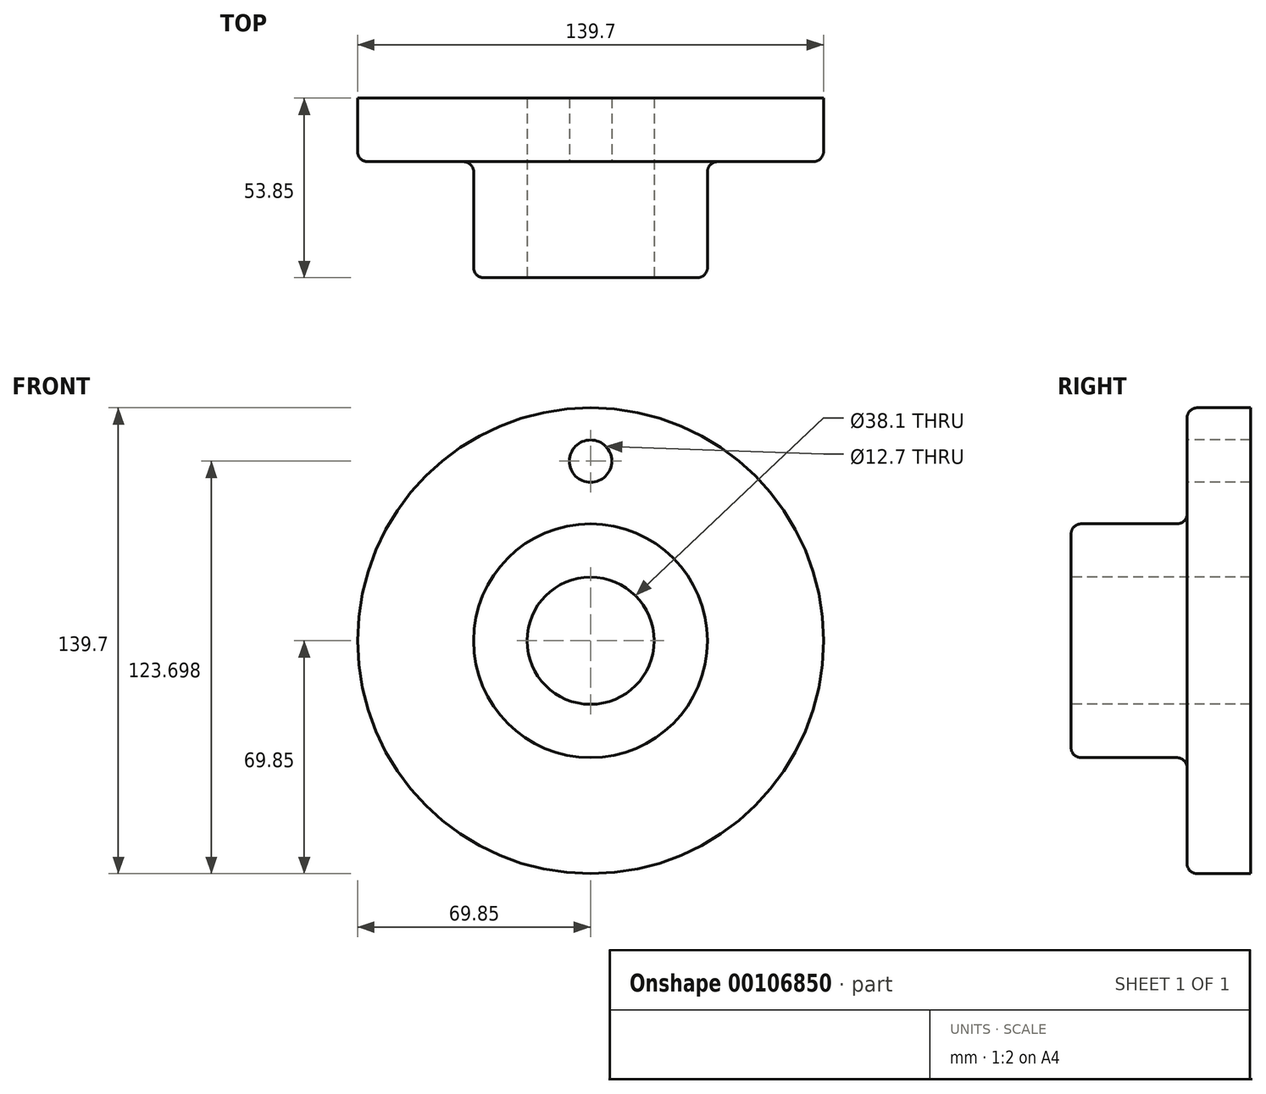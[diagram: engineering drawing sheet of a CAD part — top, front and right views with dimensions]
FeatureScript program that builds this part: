
annotation { "Feature Type Name" : "Feature", "Feature Type Description" : "" }
export const myFeature = defineFeature(function(context is Context, id is Id, definition is map)
    precondition{}
    {
        {
            var Q0;
            Q0=qCreatedBy(makeId("Right.planeOp"),FACE);
            var sketch = newSketch(context, id + "F0", { "sketchPlane" : qUnion([Q0])});
            skLineSegment(sketch, "E0", {"start": v(0, 0) * mm, "end": v(0, 35.05) * mm});
            skLineSegment(sketch, "E1", {"start": v(0, 35.05) * mm, "end": v(34.8, 35.05) * mm});
            skLineSegment(sketch, "E2", {"start": v(34.8, 35.05) * mm, "end": v(34.8, 69.85) * mm});
            skLineSegment(sketch, "E3", {"start": v(34.8, 69.85) * mm, "end": v(53.85, 69.85) * mm});
            skLineSegment(sketch, "E4", {"start": v(53.85, 69.85) * mm, "end": v(53.85, 0) * mm});
            skLineSegment(sketch, "E5", {"start": v(53.85, 0) * mm, "end": v(0, 0) * mm});
            skLineSegment(sketch, "E6", {"start": v(0, 0) * mm, "end": v(76.5, 0) * mm, "construction": true});
            skSolve(sketch);
        }
        {
            var Q0;
            Q0=makeQuery(id+"F0.imprint","IMPRINT",FACE,{"disambiguationData":[TD([[makeQuery(id+"F0.imprint","IMPRINT",EDGE,{"derivedFrom":sQuery(id+"F0.wireOp",EDGE,"E0")}),-1.0]])]});
            var Q1;
            Q1=sQuery(id+"F0.wireOp",EDGE,"E6");
            revolve(context, id + "F1", {"entities" : qUnion([Q0]), "axis" : qUnion([Q1]), "revolveType" : RevolveType.FULL});
        }
        {
            var Q0;
            Q0=qCreatedBy(makeId("Front.planeOp"),FACE);
            var sketch = newSketch(context, id + "F2", { "sketchPlane" : qUnion([Q0])});
            skCircle(sketch, "E7", {"center": v(0, 0) * mm, "radius": 19.05 * mm});
            skSolve(sketch);
        }
        {
            var Q0;
            Q0 = qSketchRegion(id + "F2", true);
            extrude(context, id + "F3", {"entities" : qUnion([Q0]), "operationType" : NewBodyOperationType.REMOVE, "endBound" : BoundingType.THROUGH_ALL, "oppositeDirection" : true, "depth" : 25.4 * mm});
        }
        {
            var Q0;
            Q0=makeQuery(id+"F1.opRevolve","SWEPT_EDGE",EDGE,{"disambiguationData":[OSD([sQuery(id+"F0.wireOp",EDGE,"E0"),sQuery(id+"F0.wireOp",EDGE,"E1")])]});
            var Q1;
            Q1=makeQuery(id+"F1.opRevolve","SWEPT_EDGE",EDGE,{"disambiguationData":[OSD([sQuery(id+"F0.wireOp",EDGE,"E1"),sQuery(id+"F0.wireOp",EDGE,"E2")])]});
            var Q2;
            Q2=makeQuery(id+"F1.opRevolve","SWEPT_EDGE",EDGE,{"disambiguationData":[OSD([sQuery(id+"F0.wireOp",EDGE,"E2"),sQuery(id+"F0.wireOp",EDGE,"E3")])]});
            fillet(context, id + "F4", {"entities" : qUnion([Q0, Q1, Q2]), "radius" : 3.05 * mm, "tangentPropagation" : true, "allowEdgeOverflow" : false});
        }
        {
            var Q0;
            Q0=makeQuery(id+"F1.opRevolve","SWEPT_FACE",FACE,{"disambiguationData":[OSD([sQuery(id+"F0.wireOp",EDGE,"E2")])]});
            var sketch = newSketch(context, id + "F5", { "sketchPlane" : qUnion([Q0])});
            skCircle(sketch, "E8", {"center": v(0, 0) * mm, "radius": 53.85 * mm, "construction": true});
            skCircle(sketch, "E9", {"center": v(0, 53.85) * mm, "radius": 6.35 * mm});
            skSolve(sketch);
        }
        {
            var Q0;
            Q0=makeQuery(id+"F5.imprint","IMPRINT",FACE,{"disambiguationData":[TD([[makeQuery(id+"F5.imprint","IMPRINT",EDGE,{"derivedFrom":sQuery(id+"F5.wireOp",EDGE,"E9")}),1.0]])]});
            extrude(context, id + "F6", {"entities" : qUnion([Q0]), "operationType" : NewBodyOperationType.REMOVE, "endBound" : BoundingType.THROUGH_ALL, "oppositeDirection" : true, "depth" : 25.4 * mm});
        }
    });
